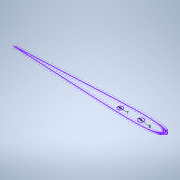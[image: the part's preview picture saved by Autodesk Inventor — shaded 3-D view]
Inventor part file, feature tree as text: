
AUTODESK INVENTOR PART (.ipt)
format: ipt  version: 2022 (Build 260153000, 153)  size: 123,392 bytes
history: native  units: mm
features: sketch x1
ambient origin geometry x8: Origin, YZ Plane, XZ Plane, XY Plane, X Axis, Y Axis, Z Axis, Center Point
feature tree (1):
  sketch  "Sketch1"  dims[d0=8.0mm d1=7.0mm]
